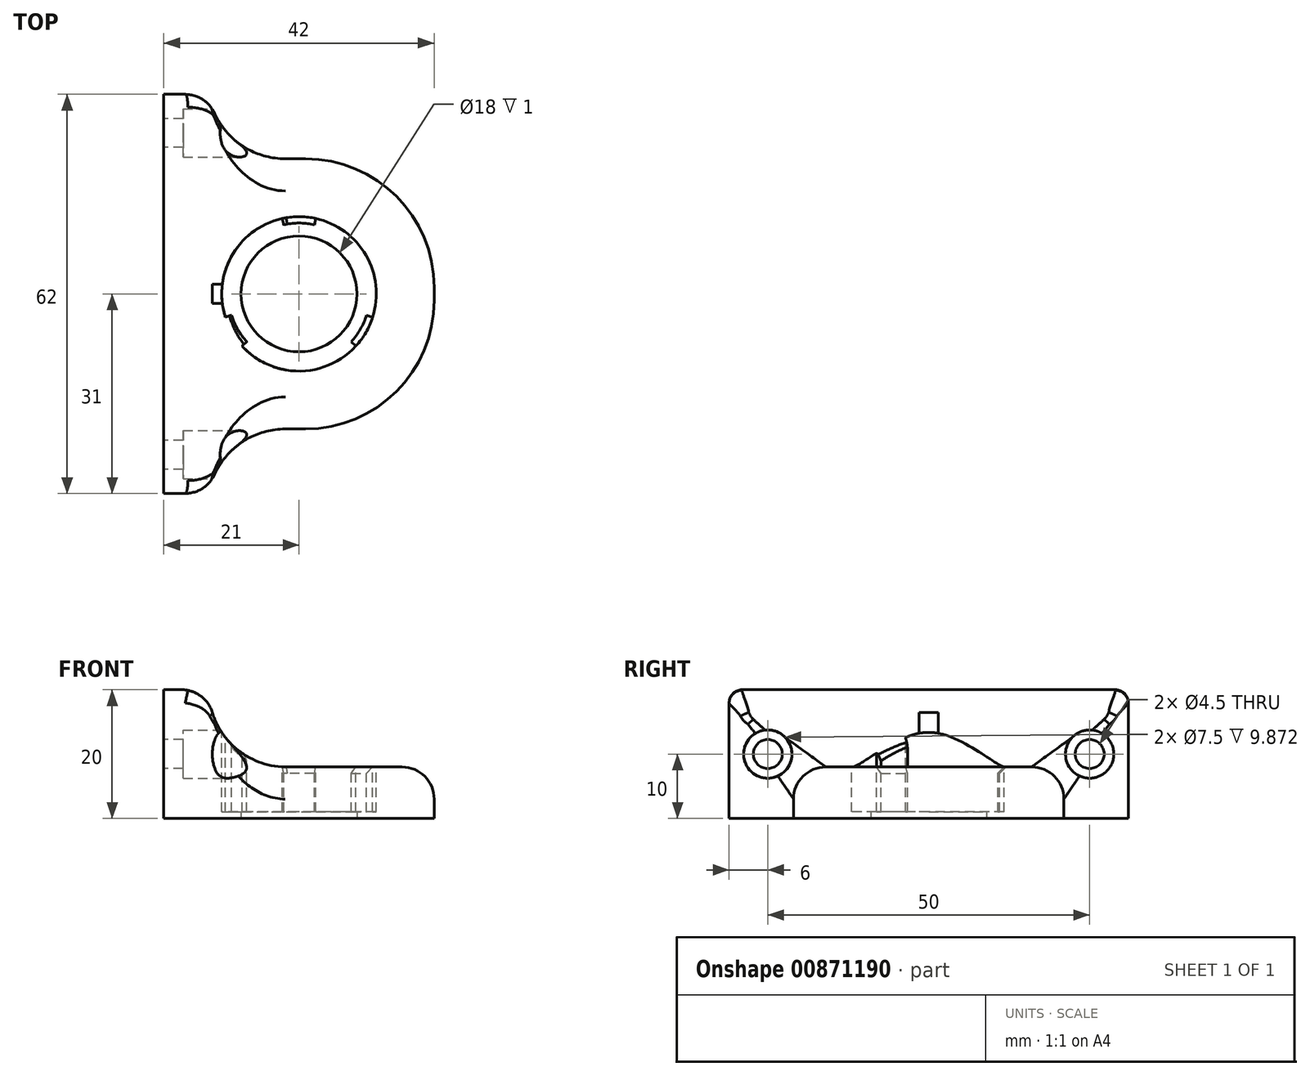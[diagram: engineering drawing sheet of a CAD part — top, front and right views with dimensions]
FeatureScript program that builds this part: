
annotation { "Feature Type Name" : "Feature", "Feature Type Description" : "" }
export const myFeature = defineFeature(function(context is Context, id is Id, definition is map)
    precondition{}
    {
        {
            var Q0;
            Q0=qCreatedBy(makeId("Top.planeOp"),FACE);
            var sketch = newSketch(context, id + "F0", { "sketchPlane" : qUnion([Q0])});
            skCircle(sketch, "E0", {"center": v(0, 0) * mm, "radius": 2.5 * mm});
            skLineSegment(sketch, "E1.bottom", {"start": v(21, 21) * mm, "end": v(-21, 21) * mm});
            skLineSegment(sketch, "E1.top", {"start": v(21, -21) * mm, "end": v(-21, -21) * mm});
            skLineSegment(sketch, "E1.left", {"start": v(21, 21) * mm, "end": v(21, -21) * mm});
            skLineSegment(sketch, "E1.right", {"start": v(-21, 21) * mm, "end": v(-21, -21) * mm});
            skPoint(sketch, "E2", {"position": v(8.8, 9.62) * mm});
            skSolve(sketch);
        }
        {
            var Q0;
            Q0=qSketchRegion(id+"F0",true);
            extrude(context, id + "F1", {"entities" : qUnion([Q0]), "depth" : 8 * mm, "offsetDistance" : 25 * mm});
        }
        {
            var Q0;
            Q0=makeQuery(id+"F1.opExtrude","CAP_FACE",FACE,{"disambiguationData":[OSD([sQuery(id+"F0.wireOp",EDGE,"E0"),sQuery(id+"F0.wireOp",EDGE,"E1.bottom"),sQuery(id+"F0.wireOp",EDGE,"E1.top"),sQuery(id+"F0.wireOp",EDGE,"E1.left"),sQuery(id+"F0.wireOp",EDGE,"E1.right"),sQuery(id+"F0.wireOp",EDGE,"SYxIzkFo-09HJ-E4OB-hM4t-ECNMrcfq3MHs"),sQuery(id+"F0.wireOp",EDGE,"LaH0diIg-dQCX-cKYX-5Nq7-zl2hJcZOabTZ"),sQuery(id+"F0.wireOp",EDGE,"bc22YLzy-SNFN-KQqS-85b7-hUGPGHNEEziu"),sQuery(id+"F0.wireOp",EDGE,"JEXjI1ur-kzYx-MYnY-67S6-5bNGs2IqBen4")])],"isStart":true});
            var sketch = newSketch(context, id + "F2", { "sketchPlane" : qUnion([Q0])});
            skLineSegment(sketch, "E3.bottom", {"start": v(-14, -31) * mm, "end": v(-21, -31) * mm});
            skLineSegment(sketch, "E3.top", {"start": v(-14, 31) * mm, "end": v(-21, 31) * mm});
            skLineSegment(sketch, "E3.left", {"start": v(-14, -31) * mm, "end": v(-14, 31) * mm});
            skLineSegment(sketch, "E3.right", {"start": v(-21, -31) * mm, "end": v(-21, 31) * mm});
            skSolve(sketch);
        }
        {
            var Q0;
            {var subQ3=sQuery(id+"F2.wireOp",EDGE,"E3.bottom");Q0=makeQuery(id+"F2.imprint","IMPRINT",FACE,{"disambiguationData":[TD([[makeQuery(id+"F2.imprint","IMPRINT",EDGE,{"derivedFrom":subQ3}),-1.0]])]});}
            var Q1;
            {var subQ0=sQuery(id+"F2.wireOp",EDGE,"E3.left");var subQ1=makeQuery(id+"F1.opExtrude","CAP_EDGE",EDGE,{"disambiguationData":[OSD([sQuery(id+"F0.wireOp",EDGE,"E1.bottom")])],"isStart":true});var subQ2=makeQuery(id+"F2.imprint","INTERSECT",VERTEX,{"derivedFrom":[subQ1,subQ0]});Q1=makeQuery(id+"F2.imprint","IMPRINT",FACE,{"disambiguationData":[TD([[makeQuery(id+"F2.imprint","IMPRINT",EDGE,{"disambiguationData":[TD([[subQ2,-1.0]])],"derivedFrom":subQ0}),1.0]])]});}
            var Q2;
            {var subQ0=sQuery(id+"F2.wireOp",EDGE,"E3.top");Q2=makeQuery(id+"F2.imprint","IMPRINT",FACE,{"disambiguationData":[TD([[makeQuery(id+"F2.imprint","IMPRINT",EDGE,{"derivedFrom":subQ0}),1.0]])]});}
            extrude(context, id + "F3", {"entities" : qUnion([Q0, Q1, Q2]), "operationType" : NewBodyOperationType.ADD, "oppositeDirection" : true, "depth" : 20 * mm, "offsetDistance" : 25 * mm});
        }
        {
            var Q0;
            Q0=makeQuery(id+"F3.opExtrude","SWEPT_FACE",FACE,{"disambiguationData":[OSD([sQuery(id+"F2.wireOp",EDGE,"E3.right")])]});
            var sketch = newSketch(context, id + "F4", { "sketchPlane" : qUnion([Q0])});
            skCircle(sketch, "E4", {"center": v(-25, 10) * mm, "radius": 2.25 * mm});
            skCircle(sketch, "E5", {"center": v(25, 10) * mm, "radius": 2.25 * mm});
            skSolve(sketch);
        }
        {
            var Q0;
            Q0=qSketchRegion(id+"F4",true);
            extrude(context, id + "F5", {"entities" : qUnion([Q0]), "operationType" : NewBodyOperationType.REMOVE, "endBound" : BoundingType.THROUGH_ALL, "oppositeDirection" : true, "depth" : 25 * mm, "offsetDistance" : 25 * mm});
        }
        {
            var Q0;
            Q0=qCreatedBy(makeId("Right.planeOp"),FACE);
            cPlane(context, id + "F6", {"entities" : qUnion([Q0]), "cplaneType" : CPlaneType.OFFSET, "offset" : 25 * mm, "width" : 150 * mm, "height" : 150 * mm});
        }
        {
            var Q0;
            Q0=qCreatedBy(id+"F6.planeOp",FACE);
            var sketch = newSketch(context, id + "F7", { "sketchPlane" : qUnion([Q0])});
            skCircle(sketch, "E6.0", {"center": v(-25, 10) * mm, "radius": 2.25 * mm});
            skCircle(sketch, "E7.0", {"center": v(25, 10) * mm, "radius": 2.25 * mm});
            skCircle(sketch, "E8", {"center": v(25, 10) * mm, "radius": 3.75 * mm});
            skCircle(sketch, "E9", {"center": v(-25, 10) * mm, "radius": 3.75 * mm});
            skSolve(sketch);
        }
        {
            var Q0;
            Q0=qSketchRegion(id+"F7",true);
            var Q1;
            Q1=makeQuery(id+"F3.opExtrude","SWEPT_FACE",FACE,{"disambiguationData":[OSD([sQuery(id+"F2.wireOp",EDGE,"E3.right")])]});
            extrude(context, id + "F8", {"entities" : qUnion([Q0]), "operationType" : NewBodyOperationType.REMOVE, "endBound" : BoundingType.UP_TO_SURFACE, "oppositeDirection" : true, "depth" : 25 * mm, "endBoundEntityFace" : qUnion([Q1]), "hasOffset" : true, "offsetDistance" : 3 * mm});
        }
        {
            var Q0;
            Q0=makeQuery(id+"F3.boolean.opBoolean","INTERSECT",EDGE,{"derivedFrom":[makeQuery(id+"F1.opExtrude","CAP_FACE",FACE,{"disambiguationData":[OSD([sQuery(id+"F0.wireOp",EDGE,"E0"),sQuery(id+"F0.wireOp",EDGE,"E1.bottom"),sQuery(id+"F0.wireOp",EDGE,"E1.top"),sQuery(id+"F0.wireOp",EDGE,"E1.left"),sQuery(id+"F0.wireOp",EDGE,"E1.right")])],"isStart":false}),makeQuery(id+"F3.opExtrude","SWEPT_FACE",FACE,{"disambiguationData":[OSD([sQuery(id+"F2.wireOp",EDGE,"E3.left")])]})]});
            var Q1;
            Q1=makeQuery(id+"F3.boolean.opBoolean","INTERSECT",EDGE,{"derivedFrom":[makeQuery(id+"F1.opExtrude","SWEPT_FACE",FACE,{"disambiguationData":[OSD([sQuery(id+"F0.wireOp",EDGE,"E1.top")])]}),makeQuery(id+"F3.opExtrude","SWEPT_FACE",FACE,{"disambiguationData":[OSD([sQuery(id+"F2.wireOp",EDGE,"E3.left")])]})]});
            var Q2;
            Q2=makeQuery(id+"F3.boolean.opBoolean","INTERSECT",EDGE,{"derivedFrom":[makeQuery(id+"F1.opExtrude","SWEPT_FACE",FACE,{"disambiguationData":[OSD([sQuery(id+"F0.wireOp",EDGE,"E1.bottom")])]}),makeQuery(id+"F3.opExtrude","SWEPT_FACE",FACE,{"disambiguationData":[OSD([sQuery(id+"F2.wireOp",EDGE,"E3.left")])]})]});
            fillet(context, id + "F9", {"entities" : qUnion([Q0, Q1, Q2]), "radius" : 12 * mm, "tangentPropagation" : true, "allowEdgeOverflow" : false});
        }
        {
            var Q0;
            Q0=makeQuery(id+"F9.opFillet","BLEND_EDGE",EDGE,{"blendedFrom":[makeQuery(id+"F3.boolean.opBoolean","INTERSECT",EDGE,{"derivedFrom":[makeQuery(id+"F1.opExtrude","SWEPT_FACE",FACE,{"disambiguationData":[OSD([sQuery(id+"F0.wireOp",EDGE,"E1.top")])]}),makeQuery(id+"F3.opExtrude","SWEPT_FACE",FACE,{"disambiguationData":[OSD([sQuery(id+"F2.wireOp",EDGE,"E3.left")])]})]}),makeQuery(id+"F3.opExtrude","SWEPT_FACE",FACE,{"disambiguationData":[OSD([sQuery(id+"F2.wireOp",EDGE,"E3.top")])]})],"blendedInto":[makeQuery(id+"F3.opExtrude","SWEPT_FACE",FACE,{"disambiguationData":[OSD([sQuery(id+"F2.wireOp",EDGE,"E3.top")])]})]});
            var Q1;
            Q1=makeQuery(id+"F3.opExtrude","CAP_EDGE",EDGE,{"disambiguationData":[OSD([sQuery(id+"F2.wireOp",EDGE,"E3.left")])],"isStart":false});
            var Q2;
            Q2=makeQuery(id+"F9.opFillet","BLEND_EDGE",EDGE,{"blendedFrom":[makeQuery(id+"F3.boolean.opBoolean","INTERSECT",EDGE,{"derivedFrom":[makeQuery(id+"F1.opExtrude","SWEPT_FACE",FACE,{"disambiguationData":[OSD([sQuery(id+"F0.wireOp",EDGE,"E1.bottom")])]}),makeQuery(id+"F3.opExtrude","SWEPT_FACE",FACE,{"disambiguationData":[OSD([sQuery(id+"F2.wireOp",EDGE,"E3.left")])]})]}),makeQuery(id+"F3.opExtrude","SWEPT_FACE",FACE,{"disambiguationData":[OSD([sQuery(id+"F2.wireOp",EDGE,"E3.bottom")])]})],"blendedInto":[makeQuery(id+"F3.opExtrude","SWEPT_FACE",FACE,{"disambiguationData":[OSD([sQuery(id+"F2.wireOp",EDGE,"E3.bottom")])]})]});
            var Q3;
            {var subQ0=makeQuery(id+"F3.opExtrude","SWEPT_FACE",FACE,{"disambiguationData":[OSD([sQuery(id+"F2.wireOp",EDGE,"E3.left")])]});var subQ1=sQuery(id+"F0.wireOp",EDGE,"E1.top");Q3=makeQuery(id+"F9.opFillet","BLEND_EDGE",EDGE,{"disambiguationData":[OD(1.0)],"blendedFrom":[makeQuery(id+"F3.boolean.opBoolean","INTERSECT",EDGE,{"derivedFrom":[makeQuery(id+"F1.opExtrude","CAP_FACE",FACE,{"disambiguationData":[OSD([sQuery(id+"F0.wireOp",EDGE,"E0"),sQuery(id+"F0.wireOp",EDGE,"E1.bottom"),subQ1,sQuery(id+"F0.wireOp",EDGE,"E1.left"),sQuery(id+"F0.wireOp",EDGE,"E1.right")])],"isStart":false}),subQ0]}),makeQuery(id+"F3.boolean.opBoolean","INTERSECT",EDGE,{"derivedFrom":[makeQuery(id+"F1.opExtrude","SWEPT_FACE",FACE,{"disambiguationData":[OSD([subQ1])]}),subQ0]})],"blendedInto":[]});}
            var Q4;
            Q4=makeQuery(id+"F1.opExtrude","CAP_EDGE",EDGE,{"disambiguationData":[OSD([sQuery(id+"F0.wireOp",EDGE,"E1.left")])],"isStart":false});
            var Q5;
            Q5=makeQuery(id+"F1.opExtrude","CAP_EDGE",EDGE,{"disambiguationData":[OSD([sQuery(id+"F0.wireOp",EDGE,"E1.bottom")])],"isStart":false});
            fillet(context, id + "F10", {"entities" : qUnion([Q0, Q1, Q2, Q3, Q4, Q5]), "radius" : 5 * mm, "tangentPropagation" : true, "allowEdgeOverflow" : false});
        }
        {
            var Q0;
            Q0=makeQuery(id+"F3.boolean.opBoolean","MERGE",FACE,{"derivedFrom":[makeQuery(id+"F1.opExtrude","CAP_FACE",FACE,{"disambiguationData":[OSD([sQuery(id+"F0.wireOp",EDGE,"E0"),sQuery(id+"F0.wireOp",EDGE,"E1.bottom"),sQuery(id+"F0.wireOp",EDGE,"E1.top"),sQuery(id+"F0.wireOp",EDGE,"E1.left"),sQuery(id+"F0.wireOp",EDGE,"E1.right")])],"isStart":true}),makeQuery(id+"F3.opExtrude","CAP_FACE",FACE,{"disambiguationData":[OSD([sQuery(id+"F2.wireOp",EDGE,"E3.bottom"),sQuery(id+"F2.wireOp",EDGE,"E3.top"),sQuery(id+"F2.wireOp",EDGE,"E3.left"),sQuery(id+"F2.wireOp",EDGE,"E3.right")])],"isStart":true})]});
            var sketch = newSketch(context, id + "F11", { "sketchPlane" : qUnion([Q0])});
            skPoint(sketch, "E10.middle", {"position": v(0, 0) * mm});
            skCircle(sketch, "E11", {"center": v(0, 0) * mm, "radius": 9 * mm});
            skSolve(sketch);
        }
        {
            var Q0;
            Q0=qSketchRegion(id+"F11",true);
            extrude(context, id + "F12", {"entities" : qUnion([Q0]), "operationType" : NewBodyOperationType.REMOVE, "endBound" : BoundingType.THROUGH_ALL, "oppositeDirection" : true, "depth" : 25 * mm, "offsetDistance" : 25 * mm});
        }
        {
            var Q0;
            Q0=qCreatedBy(makeId("Top.planeOp"),FACE);
            cPlane(context, id + "F13", {"entities" : qUnion([Q0]), "cplaneType" : CPlaneType.OFFSET, "offset" : 25 * mm, "width" : 150 * mm, "height" : 150 * mm});
        }
        {
            var Q0;
            Q0=qCreatedBy(id+"F13.planeOp",FACE);
            var sketch = newSketch(context, id + "F14", { "sketchPlane" : qUnion([Q0])});
            skArc(sketch, "E12", {"start": v(-2.6, 11.72) * mm, "mid": v(-10.4, 6) * mm, "end": v(-11.44, -3.6) * mm});
            skArc(sketch, "E13", {"start": v(-10.5, -3.3) * mm, "mid": v(-9.53, -5.5) * mm, "end": v(-8.11, -7.43) * mm});
            skLineSegment(sketch, "E14", {"start": v(2.38, 10.74) * mm, "end": v(2.6, 11.72) * mm});
            skLineSegment(sketch, "E15", {"start": v(-2.38, 10.74) * mm, "end": v(-2.6, 11.72) * mm});
            skLineSegment(sketch, "E16.1.0", {"start": v(-8.11, -7.43) * mm, "end": v(-8.85, -8.1) * mm});
            skLineSegment(sketch, "E16.1.1", {"start": v(-10.5, -3.3) * mm, "end": v(-11.44, -3.6) * mm});
            skLineSegment(sketch, "E16.2.0", {"start": v(10.5, -3.3) * mm, "end": v(11.44, -3.6) * mm});
            skLineSegment(sketch, "E16.2.1", {"start": v(8.11, -7.43) * mm, "end": v(8.85, -8.1) * mm});
            skArc(sketch, "E17.trimOffspring", {"start": v(8.11, -7.43) * mm, "mid": v(9.53, -5.5) * mm, "end": v(10.5, -3.3) * mm});
            skArc(sketch, "E18.trimOffspring", {"start": v(2.38, 10.74) * mm, "mid": v(0, 11) * mm, "end": v(-2.38, 10.74) * mm});
            skArc(sketch, "E19.trimOffspring", {"start": v(11.44, -3.6) * mm, "mid": v(10.4, 6) * mm, "end": v(2.6, 11.72) * mm});
            skArc(sketch, "E20.trimOffspring", {"start": v(-8.85, -8.1) * mm, "mid": v(0, -12) * mm, "end": v(8.85, -8.1) * mm});
            skSolve(sketch);
        }
        {
            var Q0;
            Q0 = qSketchRegion(id + "F14", true);
            var Q1;
            Q1=makeQuery(id+"F3.boolean.opBoolean","MERGE",FACE,{"derivedFrom":[makeQuery(id+"F1.opExtrude","CAP_FACE",FACE,{"disambiguationData":[OSD([sQuery(id+"F0.wireOp",EDGE,"E0"),sQuery(id+"F0.wireOp",EDGE,"E1.bottom"),sQuery(id+"F0.wireOp",EDGE,"E1.top"),sQuery(id+"F0.wireOp",EDGE,"E1.left"),sQuery(id+"F0.wireOp",EDGE,"E1.right")])],"isStart":true}),makeQuery(id+"F3.opExtrude","CAP_FACE",FACE,{"disambiguationData":[OSD([sQuery(id+"F2.wireOp",EDGE,"E3.bottom"),sQuery(id+"F2.wireOp",EDGE,"E3.top"),sQuery(id+"F2.wireOp",EDGE,"E3.left"),sQuery(id+"F2.wireOp",EDGE,"E3.right")])],"isStart":true})]});
            extrude(context, id + "F15", {"entities" : qUnion([Q0]), "operationType" : NewBodyOperationType.REMOVE, "endBound" : BoundingType.UP_TO_SURFACE, "oppositeDirection" : true, "depth" : 25 * mm, "endBoundEntityFace" : qUnion([Q1]), "hasOffset" : true, "offsetDistance" : 1 * mm});
        }
        {
            var Q0;
            {var subQ0=sQuery(id+"F2.wireOp",EDGE,"E3.left");var subQ1=sQuery(id+"F2.wireOp",EDGE,"E3.top");var subQ2=makeQuery(id+"F3.opExtrude","SWEPT_FACE",FACE,{"disambiguationData":[OSD([subQ0])]});var subQ3=sQuery(id+"F0.wireOp",EDGE,"E1.top");Q0=makeQuery(id+"F10.opFillet","BLEND_EDGE",EDGE,{"blendedFrom":[makeQuery(id+"F9.opFillet","BLEND_EDGE",EDGE,{"blendedFrom":[makeQuery(id+"F3.boolean.opBoolean","INTERSECT",EDGE,{"derivedFrom":[makeQuery(id+"F1.opExtrude","SWEPT_FACE",FACE,{"disambiguationData":[OSD([subQ3])]}),subQ2]}),makeQuery(id+"F3.opExtrude","SWEPT_FACE",FACE,{"disambiguationData":[OSD([subQ1])]})],"blendedInto":[makeQuery(id+"F3.opExtrude","SWEPT_FACE",FACE,{"disambiguationData":[OSD([subQ1])]})]}),makeQuery(id+"F9.opFillet","BLEND_EDGE",EDGE,{"disambiguationData":[OD(1.0)],"blendedFrom":[makeQuery(id+"F3.boolean.opBoolean","INTERSECT",EDGE,{"derivedFrom":[makeQuery(id+"F1.opExtrude","CAP_FACE",FACE,{"disambiguationData":[OSD([sQuery(id+"F0.wireOp",EDGE,"E0"),sQuery(id+"F0.wireOp",EDGE,"E1.bottom"),subQ3,sQuery(id+"F0.wireOp",EDGE,"E1.left"),sQuery(id+"F0.wireOp",EDGE,"E1.right")])],"isStart":false}),subQ2]}),makeQuery(id+"F3.opExtrude","CAP_FACE",FACE,{"disambiguationData":[OSD([sQuery(id+"F2.wireOp",EDGE,"E3.bottom"),subQ1,subQ0,sQuery(id+"F2.wireOp",EDGE,"E3.right")])],"isStart":false})],"blendedInto":[makeQuery(id+"F3.opExtrude","CAP_FACE",FACE,{"disambiguationData":[OSD([sQuery(id+"F2.wireOp",EDGE,"E3.bottom"),subQ1,subQ0,sQuery(id+"F2.wireOp",EDGE,"E3.right")])],"isStart":false})]})],"blendedInto":[]});}
            var Q1;
            {var subQ0=sQuery(id+"F2.wireOp",EDGE,"E3.left");var subQ1=sQuery(id+"F2.wireOp",EDGE,"E3.bottom");var subQ2=makeQuery(id+"F3.opExtrude","SWEPT_FACE",FACE,{"disambiguationData":[OSD([subQ0])]});var subQ3=sQuery(id+"F0.wireOp",EDGE,"E1.bottom");Q1=makeQuery(id+"F10.opFillet","BLEND_EDGE",EDGE,{"blendedFrom":[makeQuery(id+"F9.opFillet","BLEND_EDGE",EDGE,{"blendedFrom":[makeQuery(id+"F3.boolean.opBoolean","INTERSECT",EDGE,{"derivedFrom":[makeQuery(id+"F1.opExtrude","SWEPT_FACE",FACE,{"disambiguationData":[OSD([subQ3])]}),subQ2]}),makeQuery(id+"F3.opExtrude","SWEPT_FACE",FACE,{"disambiguationData":[OSD([subQ1])]})],"blendedInto":[makeQuery(id+"F3.opExtrude","SWEPT_FACE",FACE,{"disambiguationData":[OSD([subQ1])]})]}),makeQuery(id+"F9.opFillet","BLEND_EDGE",EDGE,{"disambiguationData":[OD(0.0)],"blendedFrom":[makeQuery(id+"F3.boolean.opBoolean","INTERSECT",EDGE,{"derivedFrom":[makeQuery(id+"F1.opExtrude","CAP_FACE",FACE,{"disambiguationData":[OSD([sQuery(id+"F0.wireOp",EDGE,"E0"),subQ3,sQuery(id+"F0.wireOp",EDGE,"E1.top"),sQuery(id+"F0.wireOp",EDGE,"E1.left"),sQuery(id+"F0.wireOp",EDGE,"E1.right")])],"isStart":false}),subQ2]}),makeQuery(id+"F3.opExtrude","CAP_FACE",FACE,{"disambiguationData":[OSD([subQ1,sQuery(id+"F2.wireOp",EDGE,"E3.top"),subQ0,sQuery(id+"F2.wireOp",EDGE,"E3.right")])],"isStart":false})],"blendedInto":[makeQuery(id+"F3.opExtrude","CAP_FACE",FACE,{"disambiguationData":[OSD([subQ1,sQuery(id+"F2.wireOp",EDGE,"E3.top"),subQ0,sQuery(id+"F2.wireOp",EDGE,"E3.right")])],"isStart":false})]})],"blendedInto":[]});}
            fillet(context, id + "F16", {"entities" : qUnion([Q0, Q1]), "radius" : 2 * mm, "tangentPropagation" : true, "allowEdgeOverflow" : false});
        }
        {
            var Q0;
            Q0=makeQuery(id+"F1.opExtrude","SWEPT_EDGE",EDGE,{"disambiguationData":[OSD([sQuery(id+"F0.wireOp",EDGE,"E1.top"),sQuery(id+"F0.wireOp",EDGE,"E1.left")])]});
            var Q1;
            Q1=makeQuery(id+"F1.opExtrude","SWEPT_EDGE",EDGE,{"disambiguationData":[OSD([sQuery(id+"F0.wireOp",EDGE,"E1.bottom"),sQuery(id+"F0.wireOp",EDGE,"E1.left")])]});
            fillet(context, id + "F17", {"entities" : qUnion([Q0, Q1]), "radius" : 20 * mm, "tangentPropagation" : true, "allowEdgeOverflow" : false});
        }
        {
            var Q0;
            Q0=makeQuery(id+"F15.boolean.opBoolean","INTERSECT",EDGE,{"derivedFrom":[makeQuery(id+"F1.opExtrude","CAP_FACE",FACE,{"disambiguationData":[OSD([sQuery(id+"F0.wireOp",EDGE,"E0"),sQuery(id+"F0.wireOp",EDGE,"E1.bottom"),sQuery(id+"F0.wireOp",EDGE,"E1.top"),sQuery(id+"F0.wireOp",EDGE,"E1.left"),sQuery(id+"F0.wireOp",EDGE,"E1.right")])],"isStart":false}),makeQuery(id+"F15.opExtrude","SWEPT_FACE",FACE,{"disambiguationData":[OSD([sQuery(id+"F14.wireOp",EDGE,"E17.trimOffspring")])]})]});
            var Q1;
            Q1=makeQuery(id+"F15.boolean.opBoolean","INTERSECT",EDGE,{"derivedFrom":[makeQuery(id+"F9.opFillet","BLEND_FACE",FACE,{"disambiguationData":[OSD([sQuery(id+"F0.wireOp",EDGE,"E0"),sQuery(id+"F0.wireOp",EDGE,"E1.bottom"),sQuery(id+"F0.wireOp",EDGE,"E1.top"),sQuery(id+"F0.wireOp",EDGE,"E1.left"),sQuery(id+"F0.wireOp",EDGE,"E1.right"),sQuery(id+"F2.wireOp",EDGE,"E3.left")]),OD(2.0)]}),makeQuery(id+"F15.opExtrude","SWEPT_FACE",FACE,{"disambiguationData":[OSD([sQuery(id+"F14.wireOp",EDGE,"E13")])]})]});
            var Q2;
            Q2=makeQuery(id+"F15.boolean.opBoolean","INTERSECT",EDGE,{"derivedFrom":[makeQuery(id+"F1.opExtrude","CAP_FACE",FACE,{"disambiguationData":[OSD([sQuery(id+"F0.wireOp",EDGE,"E0"),sQuery(id+"F0.wireOp",EDGE,"E1.bottom"),sQuery(id+"F0.wireOp",EDGE,"E1.top"),sQuery(id+"F0.wireOp",EDGE,"E1.left"),sQuery(id+"F0.wireOp",EDGE,"E1.right")])],"isStart":false}),makeQuery(id+"F15.opExtrude","SWEPT_FACE",FACE,{"disambiguationData":[OSD([sQuery(id+"F14.wireOp",EDGE,"E18.trimOffspring")])]})]});
            chamfer(context, id + "F18", {"entities" : qUnion([Q0, Q1, Q2]), "width" : 1 * mm, "tangentPropagation" : true});
        }
    });
